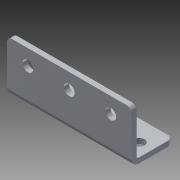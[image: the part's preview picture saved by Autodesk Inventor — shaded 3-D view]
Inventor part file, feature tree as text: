
AUTODESK INVENTOR PART (.ipt)
format: ipt  version: 2013 (Build 170138000, 138)  size: 189,440 bytes
history: native  units: in
note: dims shown in document units (in); Inventor stores cm internally (conversion verified against a paired STEP export)
features: sheet_metal_op x4, other x4, sketch x3, chamfer x1
ambient origin geometry x8: Origin, YZ Plane, XZ Plane, XY Plane, X Axis, Y Axis, Z Axis, Center Point
bodies: Solid1 (feature_tree)
feature tree (12):
  sheet_metal_op  "Face1"
  sheet_metal_op  "Flange1"
  chamfer  "Corner Round1"
  sketch  "Sketch1"  dims[d0=3.0in]
  other  "Plate1"
  sketch  "Sketch2"  dims[d1=1.0in]
  other  "Plate2"
  sheet_metal_op  "Bend1"
  sheet_metal_op  "Corner1"
  sketch  "Sketch3"  dims[d2=0.26in d3=2.375in d4=0.125in d5=0.125in d6=0.0625in d7=0.25in d8=0.125in d9=1.25in d10=90.0deg d11=0.05in d12=0.5in d13=0.125in d14=0.125in d15=2.0in d17=0.26in d19=0.875in d20=0.125in d21=0.0in d22=0.125in]
  other  "Cut1"
  other  "Definition1"
